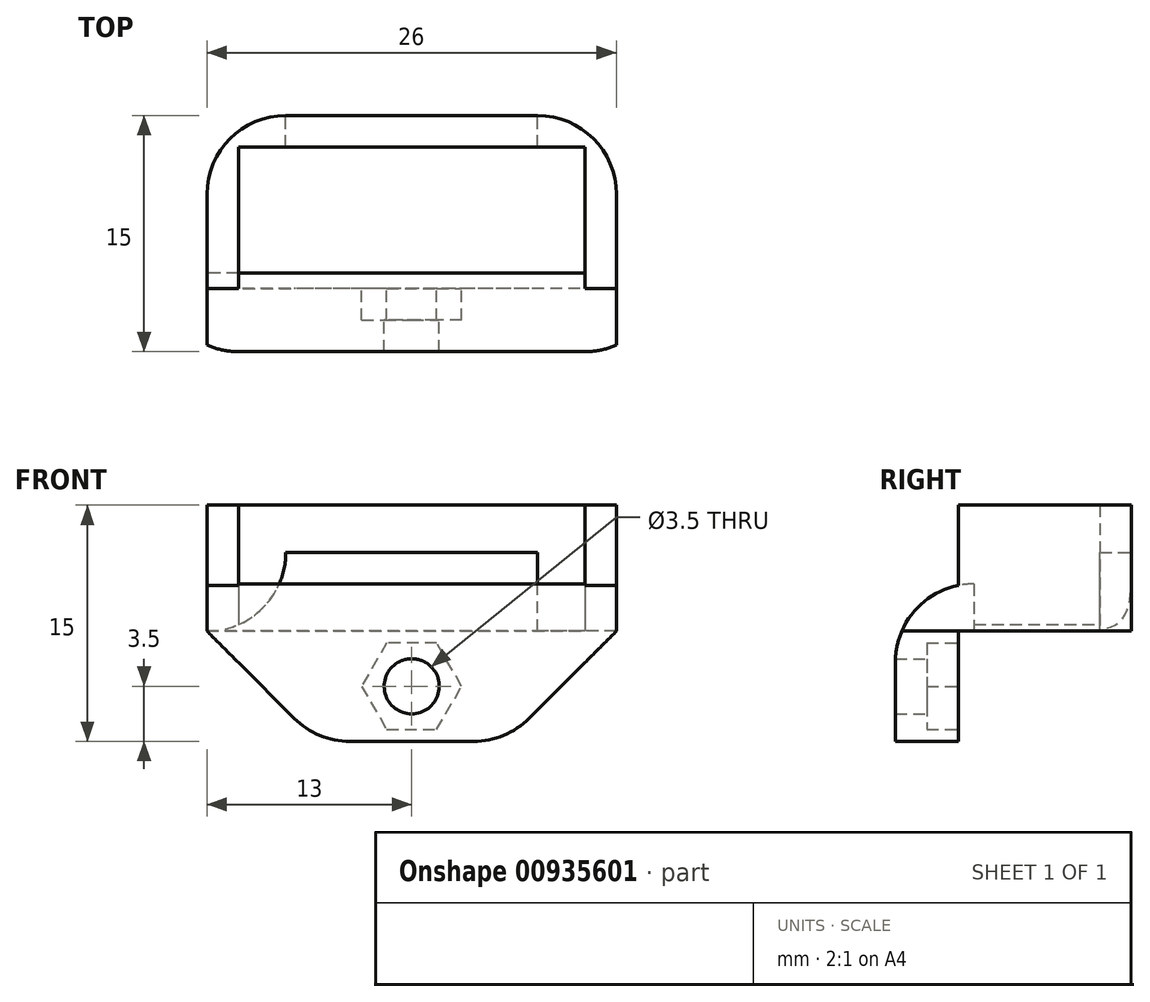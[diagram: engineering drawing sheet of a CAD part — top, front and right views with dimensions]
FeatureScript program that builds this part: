
annotation { "Feature Type Name" : "Feature", "Feature Type Description" : "" }
export const myFeature = defineFeature(function(context is Context, id is Id, definition is map)
    precondition{}
    {
        {
            var Q0;
            Q0=qCreatedBy(makeId("Top.planeOp"),FACE);
            var sketch = newSketch(context, id + "F0", { "sketchPlane" : qUnion([Q0])});
            skLineSegment(sketch, "E0.bottom", {"start": v(13, 7.5) * mm, "end": v(-13, 7.5) * mm});
            skLineSegment(sketch, "E0.top", {"start": v(13, -7.5) * mm, "end": v(-13, -7.5) * mm});
            skLineSegment(sketch, "E0.left", {"start": v(13, 7.5) * mm, "end": v(13, -7.5) * mm});
            skLineSegment(sketch, "E0.right", {"start": v(-13, 7.5) * mm, "end": v(-13, -7.5) * mm});
            skPoint(sketch, "E0.middle", {"position": v(0, 0) * mm});
            skLineSegment(sketch, "E1", {"start": v(-11, -2.5) * mm, "end": v(11, -2.5) * mm});
            skLineSegment(sketch, "E2.bottom", {"start": v(7.5, -7.5) * mm, "end": v(-7.5, -7.5) * mm});
            skLineSegment(sketch, "E2.top", {"start": v(7.5, -3.5) * mm, "end": v(-7.5, -3.5) * mm});
            skPoint(sketch, "E2.middle", {"position": v(0, -5.5) * mm});
            skLineSegment(sketch, "E3.bottom", {"start": v(11, -7.5) * mm, "end": v(-11, -7.5) * mm});
            skLineSegment(sketch, "E3.top", {"start": v(11, 5.5) * mm, "end": v(-11, 5.5) * mm});
            skLineSegment(sketch, "E3.left", {"start": v(11, -3.5) * mm, "end": v(11, 5.5) * mm});
            skLineSegment(sketch, "E3.right", {"start": v(-11, -3.5) * mm, "end": v(-11, 5.5) * mm});
            skPoint(sketch, "E3.middle", {"position": v(0, -1) * mm});
            skLineSegment(sketch, "E4", {"start": v(-7.5, -3.5) * mm, "end": v(-11, -3.5) * mm});
            skLineSegment(sketch, "E5", {"start": v(7.5, -3.5) * mm, "end": v(11, -3.5) * mm});
            skLineSegment(sketch, "E6", {"start": v(-11, -3.5) * mm, "end": v(-13, -3.5) * mm});
            skLineSegment(sketch, "E7", {"start": v(11, -3.5) * mm, "end": v(13, -3.5) * mm});
            skSolve(sketch);
        }
        {
            var Q0;
            {var subQ9=sQuery(id+"F0.wireOp",EDGE,"E0.bottom");Q0=makeQuery(id+"F0.imprint","IMPRINT",FACE,{"disambiguationData":[TD([[makeQuery(id+"F0.imprint","IMPRINT",EDGE,{"derivedFrom":subQ9}),1.0]])]});}
            extrude(context, id + "F1", {"entities" : qUnion([Q0]), "depth" : 8 * mm, "offsetDistance" : 25 * mm});
        }
        {
            var Q0;
            {var subQ2=sQuery(id+"F0.wireOp",EDGE,"E1");Q0=makeQuery(id+"F0.imprint","IMPRINT",FACE,{"disambiguationData":[TD([[makeQuery(id+"F0.imprint","IMPRINT",EDGE,{"derivedFrom":subQ2}),-1.0]])]});}
            var Q1;
            Q1=makeQuery(id+"F0.imprint","IMPRINT",FACE,{"disambiguationData":[TD([[makeQuery(id+"F0.imprint","IMPRINT",EDGE,{"derivedFrom":sQuery(id+"F0.wireOp",EDGE,"E2.top")}),1.0]])]});
            extrude(context, id + "F2", {"entities" : qUnion([Q0, Q1]), "depth" : 3 * mm, "offsetDistance" : 25 * mm});
        }
        {
            var Q0;
            Q0=makeQuery(id+"F1.opExtrude","SWEPT_FACE",FACE,{"disambiguationData":[OSD([sQuery(id+"F0.wireOp",EDGE,"E0.bottom")])]});
            var sketch = newSketch(context, id + "F3", { "sketchPlane" : qUnion([Q0])});
            skLineSegment(sketch, "E8.bottom", {"start": v(8, 0) * mm, "end": v(-8, 0) * mm});
            skLineSegment(sketch, "E8.top", {"start": v(8, 5) * mm, "end": v(-8, 5) * mm});
            skLineSegment(sketch, "E8.left", {"start": v(8, 0) * mm, "end": v(8, 5) * mm});
            skLineSegment(sketch, "E8.right", {"start": v(-8, 0) * mm, "end": v(-8, 5) * mm});
            skPoint(sketch, "E8.middle", {"position": v(0, 2.5) * mm});
            skSolve(sketch);
        }
        {
            var Q0;
            Q0=makeQuery(id+"F3.imprint","IMPRINT",FACE,{"disambiguationData":[TD([[makeQuery(id+"F3.imprint","IMPRINT",EDGE,{"derivedFrom":sQuery(id+"F3.wireOp",EDGE,"E8.bottom")}),1.0]])]});
            extrude(context, id + "F4", {"entities" : qUnion([Q0]), "operationType" : NewBodyOperationType.REMOVE, "endBound" : BoundingType.UP_TO_NEXT, "oppositeDirection" : true, "depth" : 25 * mm, "offsetDistance" : 25 * mm});
        }
        {
            var Q0;
            Q0=makeQuery(id+"F0.imprint","IMPRINT",FACE,{"disambiguationData":[TD([[makeQuery(id+"F0.imprint","IMPRINT",EDGE,{"derivedFrom":sQuery(id+"F0.wireOp",EDGE,"E2.top")}),1.0]])]});
            extrude(context, id + "F5", {"entities" : qUnion([Q0]), "operationType" : NewBodyOperationType.ADD, "oppositeDirection" : true, "depth" : 7 * mm, "offsetDistance" : 25 * mm});
        }
        {
            var Q0;
            Q0=makeQuery(id+"F5.opExtrude","CAP_EDGE",EDGE,{"disambiguationData":[OSD([sQuery(id+"F0.wireOp",EDGE,"E0.left")])],"isStart":false});
            var Q1;
            Q1=makeQuery(id+"F5.opExtrude","CAP_EDGE",EDGE,{"disambiguationData":[OSD([sQuery(id+"F0.wireOp",EDGE,"E0.right")])],"isStart":false});
            chamfer(context, id + "F6", {"entities" : qUnion([Q0, Q1]), "width" : 7 * mm, "tangentPropagation" : true});
        }
        {
            var Q0;
            {var subQ0=sQuery(id+"F0.wireOp",EDGE,"E7");var subQ1=sQuery(id+"F0.wireOp",EDGE,"E6");Q0=makeQuery(id+"F5.boolean.opBoolean","MERGE",FACE,{"derivedFrom":[makeQuery(id+"F2.opExtrude","SWEPT_FACE",FACE,{"disambiguationData":[OSD([subQ1])]}),makeQuery(id+"F2.opExtrude","SWEPT_FACE",FACE,{"disambiguationData":[OSD([subQ0])]}),makeQuery(id+"F5.opExtrude","SWEPT_FACE",FACE,{"disambiguationData":[OSD([sQuery(id+"F0.wireOp",EDGE,"E2.top"),sQuery(id+"F0.wireOp",EDGE,"E4"),sQuery(id+"F0.wireOp",EDGE,"E5"),subQ1,subQ0])]})]});}
            var sketch = newSketch(context, id + "F7", { "sketchPlane" : qUnion([Q0])});
            skCircle(sketch, "E9.cCircle", {"center": v(0, -3.5) * mm, "radius": 2.75 * mm, "construction": true});
            skLineSegment(sketch, "E9.0", {"start": v(3.18, -3.5) * mm, "end": v(1.59, -6.25) * mm});
            skLineSegment(sketch, "E9.1", {"start": v(1.59, -6.25) * mm, "end": v(-1.59, -6.25) * mm});
            skLineSegment(sketch, "E9.2", {"start": v(-1.59, -6.25) * mm, "end": v(-3.18, -3.5) * mm});
            skLineSegment(sketch, "E9.3", {"start": v(-3.18, -3.5) * mm, "end": v(-1.59, -0.75) * mm});
            skLineSegment(sketch, "E9.4", {"start": v(-1.59, -0.75) * mm, "end": v(1.59, -0.75) * mm});
            skLineSegment(sketch, "E9.5", {"start": v(1.59, -0.75) * mm, "end": v(3.18, -3.5) * mm});
            skPoint(sketch, "E9.0.midPoint", {"position": v(2.38, -4.88) * mm});
            skCircle(sketch, "E10", {"center": v(0, -3.5) * mm, "radius": 1.75 * mm});
            skSolve(sketch);
        }
        {
            var Q0;
            Q0=makeQuery(id+"F7.imprint","IMPRINT",FACE,{"disambiguationData":[TD([[makeQuery(id+"F7.imprint","IMPRINT",EDGE,{"derivedFrom":sQuery(id+"F7.wireOp",EDGE,"E10")}),1.0]])]});
            extrude(context, id + "F8", {"entities" : qUnion([Q0]), "operationType" : NewBodyOperationType.REMOVE, "endBound" : BoundingType.THROUGH_ALL, "oppositeDirection" : true, "depth" : 25 * mm, "offsetDistance" : 25 * mm});
        }
        {
            var Q0;
            Q0=makeQuery(id+"F7.imprint","IMPRINT",FACE,{"disambiguationData":[TD([[makeQuery(id+"F7.imprint","IMPRINT",EDGE,{"derivedFrom":sQuery(id+"F7.wireOp",EDGE,"E9.0")}),-1.0]])]});
            extrude(context, id + "F9", {"entities" : qUnion([Q0]), "operationType" : NewBodyOperationType.REMOVE, "oppositeDirection" : true, "depth" : 2 * mm, "offsetDistance" : 25 * mm});
        }
        {
            var Q0;
            Q0=makeQuery(id+"F4.boolean.opBoolean","COPY",EDGE,{"derivedFrom":makeQuery(id+"F4.opExtrude","SWEPT_EDGE",EDGE,{"disambiguationData":[OSD([sQuery(id+"F0.wireOp",EDGE,"E0.bottom"),sQuery(id+"F3.wireOp",EDGE,"E8.bottom"),sQuery(id+"F3.wireOp",EDGE,"E8.right")])]})});
            var Q1;
            Q1=makeQuery(id+"F4.boolean.opBoolean","COPY",EDGE,{"derivedFrom":makeQuery(id+"F4.opExtrude","SWEPT_EDGE",EDGE,{"disambiguationData":[OSD([sQuery(id+"F0.wireOp",EDGE,"E0.bottom"),sQuery(id+"F3.wireOp",EDGE,"E8.bottom"),sQuery(id+"F3.wireOp",EDGE,"E8.left")])]})});
            fillet(context, id + "F10", {"entities" : qUnion([Q0, Q1]), "radius" : 5 * mm, "tangentPropagation" : true, "allowEdgeOverflow" : false});
        }
        {
            var Q0;
            Q0=makeQuery(id+"F1.opExtrude","SWEPT_EDGE",EDGE,{"disambiguationData":[OSD([sQuery(id+"F0.wireOp",EDGE,"E0.bottom"),sQuery(id+"F0.wireOp",EDGE,"E0.right")])]});
            var Q1;
            Q1=makeQuery(id+"F1.opExtrude","SWEPT_EDGE",EDGE,{"disambiguationData":[OSD([sQuery(id+"F0.wireOp",EDGE,"E0.bottom"),sQuery(id+"F0.wireOp",EDGE,"E0.left")])]});
            var Q2;
            {var subQ0=sQuery(id+"F0.wireOp",EDGE,"E0.left");Q2=makeQuery(id+"F6.opChamfer","BLEND_EDGE",EDGE,{"blendedFrom":[makeQuery(id+"F5.opExtrude","CAP_EDGE",EDGE,{"disambiguationData":[OSD([subQ0])],"isStart":false}),makeQuery(id+"F5.opExtrude","CAP_FACE",FACE,{"disambiguationData":[OSD([sQuery(id+"F0.wireOp",EDGE,"E0.top"),subQ0,sQuery(id+"F0.wireOp",EDGE,"E0.right"),sQuery(id+"F0.wireOp",EDGE,"E2.top"),sQuery(id+"F0.wireOp",EDGE,"E3.bottom"),sQuery(id+"F0.wireOp",EDGE,"E4"),sQuery(id+"F0.wireOp",EDGE,"E5"),sQuery(id+"F0.wireOp",EDGE,"E6"),sQuery(id+"F0.wireOp",EDGE,"E7")])],"isStart":false})],"blendedInto":[makeQuery(id+"F5.opExtrude","CAP_FACE",FACE,{"disambiguationData":[OSD([sQuery(id+"F0.wireOp",EDGE,"E0.top"),subQ0,sQuery(id+"F0.wireOp",EDGE,"E0.right"),sQuery(id+"F0.wireOp",EDGE,"E2.top"),sQuery(id+"F0.wireOp",EDGE,"E3.bottom"),sQuery(id+"F0.wireOp",EDGE,"E4"),sQuery(id+"F0.wireOp",EDGE,"E5"),sQuery(id+"F0.wireOp",EDGE,"E6"),sQuery(id+"F0.wireOp",EDGE,"E7")])],"isStart":false})]});}
            var Q3;
            {var subQ0=sQuery(id+"F0.wireOp",EDGE,"E0.right");Q3=makeQuery(id+"F6.opChamfer","BLEND_EDGE",EDGE,{"blendedFrom":[makeQuery(id+"F5.opExtrude","CAP_EDGE",EDGE,{"disambiguationData":[OSD([subQ0])],"isStart":false}),makeQuery(id+"F5.opExtrude","CAP_FACE",FACE,{"disambiguationData":[OSD([sQuery(id+"F0.wireOp",EDGE,"E0.top"),sQuery(id+"F0.wireOp",EDGE,"E0.left"),subQ0,sQuery(id+"F0.wireOp",EDGE,"E2.top"),sQuery(id+"F0.wireOp",EDGE,"E3.bottom"),sQuery(id+"F0.wireOp",EDGE,"E4"),sQuery(id+"F0.wireOp",EDGE,"E5"),sQuery(id+"F0.wireOp",EDGE,"E6"),sQuery(id+"F0.wireOp",EDGE,"E7")])],"isStart":false})],"blendedInto":[makeQuery(id+"F5.opExtrude","CAP_FACE",FACE,{"disambiguationData":[OSD([sQuery(id+"F0.wireOp",EDGE,"E0.top"),sQuery(id+"F0.wireOp",EDGE,"E0.left"),subQ0,sQuery(id+"F0.wireOp",EDGE,"E2.top"),sQuery(id+"F0.wireOp",EDGE,"E3.bottom"),sQuery(id+"F0.wireOp",EDGE,"E4"),sQuery(id+"F0.wireOp",EDGE,"E5"),sQuery(id+"F0.wireOp",EDGE,"E6"),sQuery(id+"F0.wireOp",EDGE,"E7")])],"isStart":false})]});}
            var Q4;
            Q4=makeQuery(id+"F2.opExtrude","CAP_EDGE",EDGE,{"disambiguationData":[OSD([sQuery(id+"F0.wireOp",EDGE,"E0.top"),sQuery(id+"F0.wireOp",EDGE,"E3.bottom")])],"isStart":false});
            fillet(context, id + "F11", {"entities" : qUnion([Q0, Q1, Q2, Q3, Q4]), "radius" : 5 * mm, "tangentPropagation" : true, "allowEdgeOverflow" : false});
        }
    });
